# Revit family: S-31
name_source: partatom
category: Pipe Fittings
revit_build: Autodesk Revit 2015 (Build: 20140606_1530(x64)
units: mm (PartAtom-declared; Revit-internal decimal feet)

## types (3) — shared parameters
Aplicación = LAVABO, BIDET
Caudal = 0.4 L/s
Description = SIFON CURVO EXTENSIBLE, SALIDA HORIZONTAL, RACOR CON JUNTA FIX
Manufacturer = Jimten
Material = PP (Blanco)
Model = S-31
URL = http://www.jimten.com

## per-type parameters (varying)
| type | Amax | Amin | Entradas | Referencia | S | Salida | r |
| S-31_1 1/2" | 230 mm  [stored 0.754593 ft] | 170 mm  [stored 0.557743 ft] | 1 1/2'' ROSCA HEMBRA | 006028 | 40 mm  [stored 0.131234 ft] | Ø40 MM (HEMBRA) | 38 mm |
| S-31_1 1/4" x 1 1/2" | 230 mm  [stored 0.754593 ft] | 170 mm  [stored 0.557743 ft] | 1 1/4'' ROSCA HEMBRA | 006366 | 40 mm  [stored 0.131234 ft] | Ø40 MM (HEMBRA) | 32 mm  [stored 0.104987 ft] |
| S-31_1 1/4" | 210 mm  [stored 0.688976 ft] | 163 mm  [stored 0.534777 ft] | 1 1/4'' ROSCA HEMBRA | 006046 | 32 mm  [stored 0.104987 ft] | Ø32 MM (HEMBRA) | 32 mm  [stored 0.104987 ft] |

note: [stored X ft] marks values corroborated as IEEE doubles in the binary element streams (Revit-internal decimal feet)
